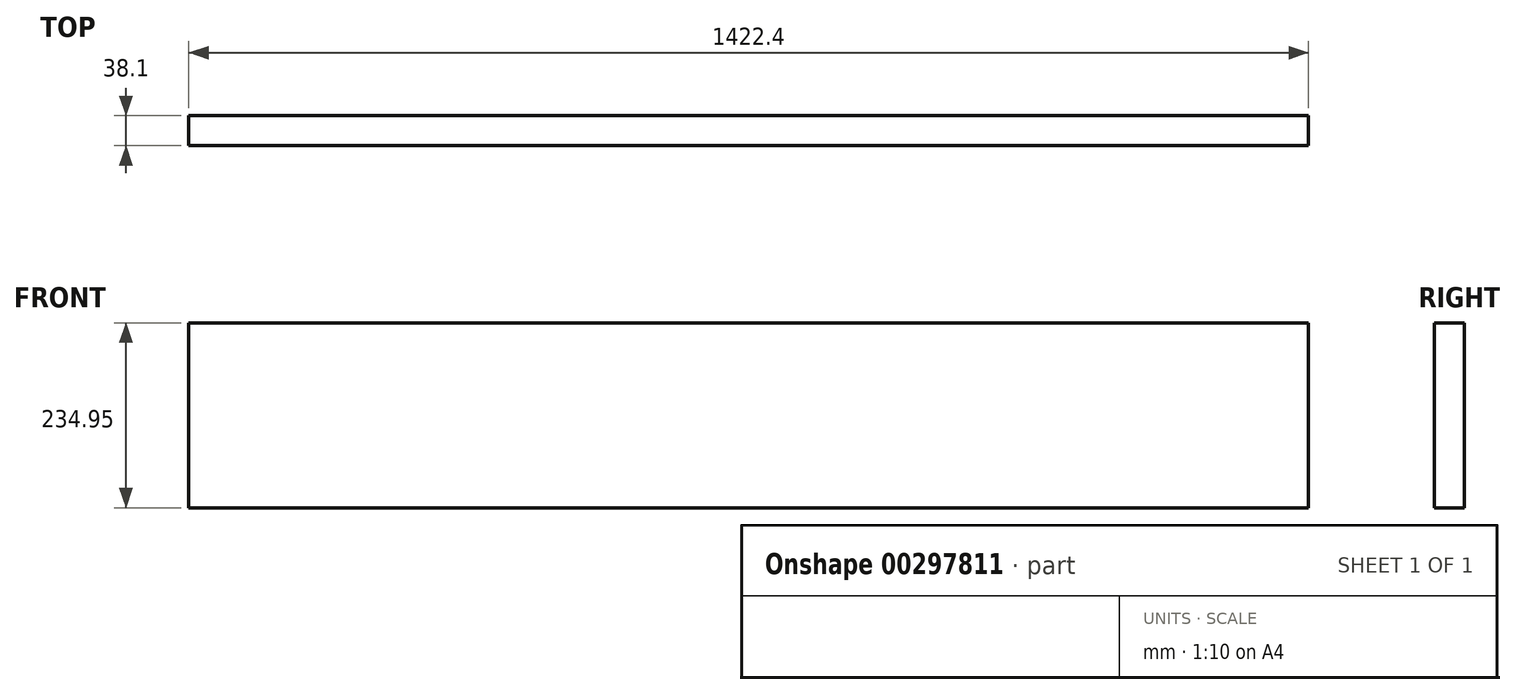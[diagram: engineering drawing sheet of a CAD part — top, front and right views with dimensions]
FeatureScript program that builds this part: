
annotation { "Feature Type Name" : "Feature", "Feature Type Description" : "" }
export const myFeature = defineFeature(function(context is Context, id is Id, definition is map)
    precondition{}
    {
        {
            var Q0;
            Q0=qCreatedBy(makeId("Front.planeOp"),FACE);
            var sketch = newSketch(context, id + "F0", { "sketchPlane" : qUnion([Q0])});
            skLineSegment(sketch, "E0.bottom", {"start": v(0, 0) * mm, "end": v(1422.4, 0) * mm});
            skLineSegment(sketch, "E0.top", {"start": v(0, 234.95) * mm, "end": v(1422.4, 234.95) * mm});
            skLineSegment(sketch, "E0.left", {"start": v(0, 0) * mm, "end": v(0, 234.95) * mm});
            skLineSegment(sketch, "E0.right", {"start": v(1422.4, 0) * mm, "end": v(1422.4, 234.95) * mm});
            skSolve(sketch);
        }
        {
            var Q0;
            Q0=makeQuery(id+"F0.imprint","IMPRINT",FACE,{"disambiguationData":[TD([[makeQuery(id+"F0.imprint","IMPRINT",EDGE,{"derivedFrom":sQuery(id+"F0.wireOp",EDGE,"E0.bottom")}),1.0]])]});
            extrude(context, id + "F1", {"entities" : qUnion([Q0]), "depth" : 38.1 * mm});
        }
    });
